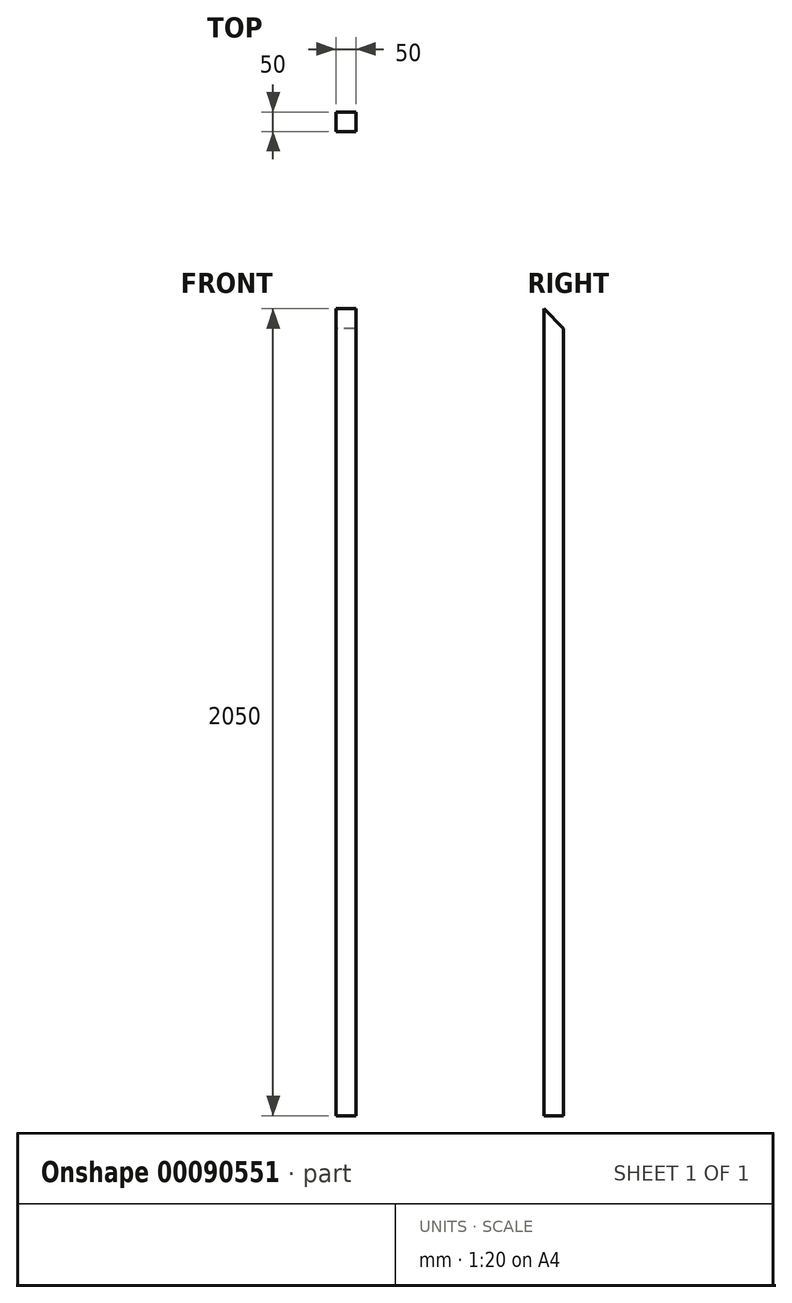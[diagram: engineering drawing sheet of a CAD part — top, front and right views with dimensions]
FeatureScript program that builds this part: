
annotation { "Feature Type Name" : "Feature", "Feature Type Description" : "" }
export const myFeature = defineFeature(function(context is Context, id is Id, definition is map)
    precondition{}
    {
        {
            var Q0;
            Q0=qCreatedBy(makeId("Top.planeOp"),FACE);
            var sketch = newSketch(context, id + "F0", { "sketchPlane" : qUnion([Q0])});
            skLineSegment(sketch, "E0.bottom", {"start": v(25, -25) * mm, "end": v(-25, -25) * mm});
            skLineSegment(sketch, "E0.top", {"start": v(25, 25) * mm, "end": v(-25, 25) * mm});
            skLineSegment(sketch, "E0.left", {"start": v(25, -25) * mm, "end": v(25, 25) * mm});
            skLineSegment(sketch, "E0.right", {"start": v(-25, -25) * mm, "end": v(-25, 25) * mm});
            skPoint(sketch, "E0.middle", {"position": v(0, 0) * mm});
            skSolve(sketch);
        }
        {
            var Q0;
            Q0 = qSketchRegion(id + "F0", true);
            extrude(context, id + "F1", {"entities" : qUnion([Q0]), "depth" : 2050 * mm});
        }
        {
            var Q0;
            Q0=qCreatedBy(makeId("Right.planeOp"),FACE);
            var sketch = newSketch(context, id + "F2", { "sketchPlane" : qUnion([Q0])});
            skLineSegment(sketch, "E1", {"start": v(-25, 2050) * mm, "end": v(135.3, 2050) * mm});
            skLineSegment(sketch, "E2", {"start": v(135.3, 2050) * mm, "end": v(135.3, 1889.7) * mm});
            skLineSegment(sketch, "E3", {"start": v(135.3, 1889.7) * mm, "end": v(-25, 2050) * mm});
            skSolve(sketch);
        }
        {
            var Q0;
            Q0 = qSketchRegion(id + "F2", true);
            extrude(context, id + "F3", {"entities" : qUnion([Q0]), "operationType" : NewBodyOperationType.REMOVE, "endBound" : BoundingType.THROUGH_ALL, "oppositeDirection" : true, "depth" : 25 * mm, "hasSecondDirection" : true, "secondDirectionBound" : SecondDirectionBoundingType.THROUGH_ALL, "secondDirectionOppositeDirection" : false, "secondDirectionDepth" : 25 * mm});
        }
    });
